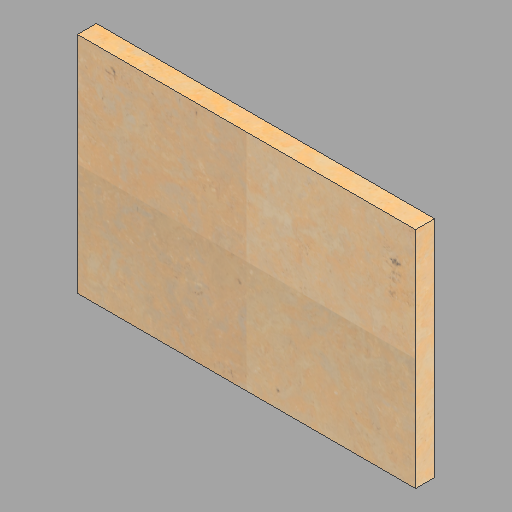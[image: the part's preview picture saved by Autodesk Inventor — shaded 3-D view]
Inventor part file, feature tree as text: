
AUTODESK INVENTOR PART (.ipt)
format: ipt  version: 2023 (Build 270158000, 158)  size: 285,696 bytes
history: native  units: in
note: dims shown in document units (in); Inventor stores cm internally (conversion verified against a paired STEP export)
features: extrude x1, sketch x1
ambient origin geometry x8: Origin, YZ Plane, XZ Plane, XY Plane, X Axis, Y Axis, Z Axis, Center Point
bodies: Solid1 (feature_tree)
feature tree (2):
  extrude  "Extrusion1"  Depth=23.625in
  sketch  "Sketch1"  dims[d0=35.625in d1=23.625in d2=2.0in d3=0.0in]
